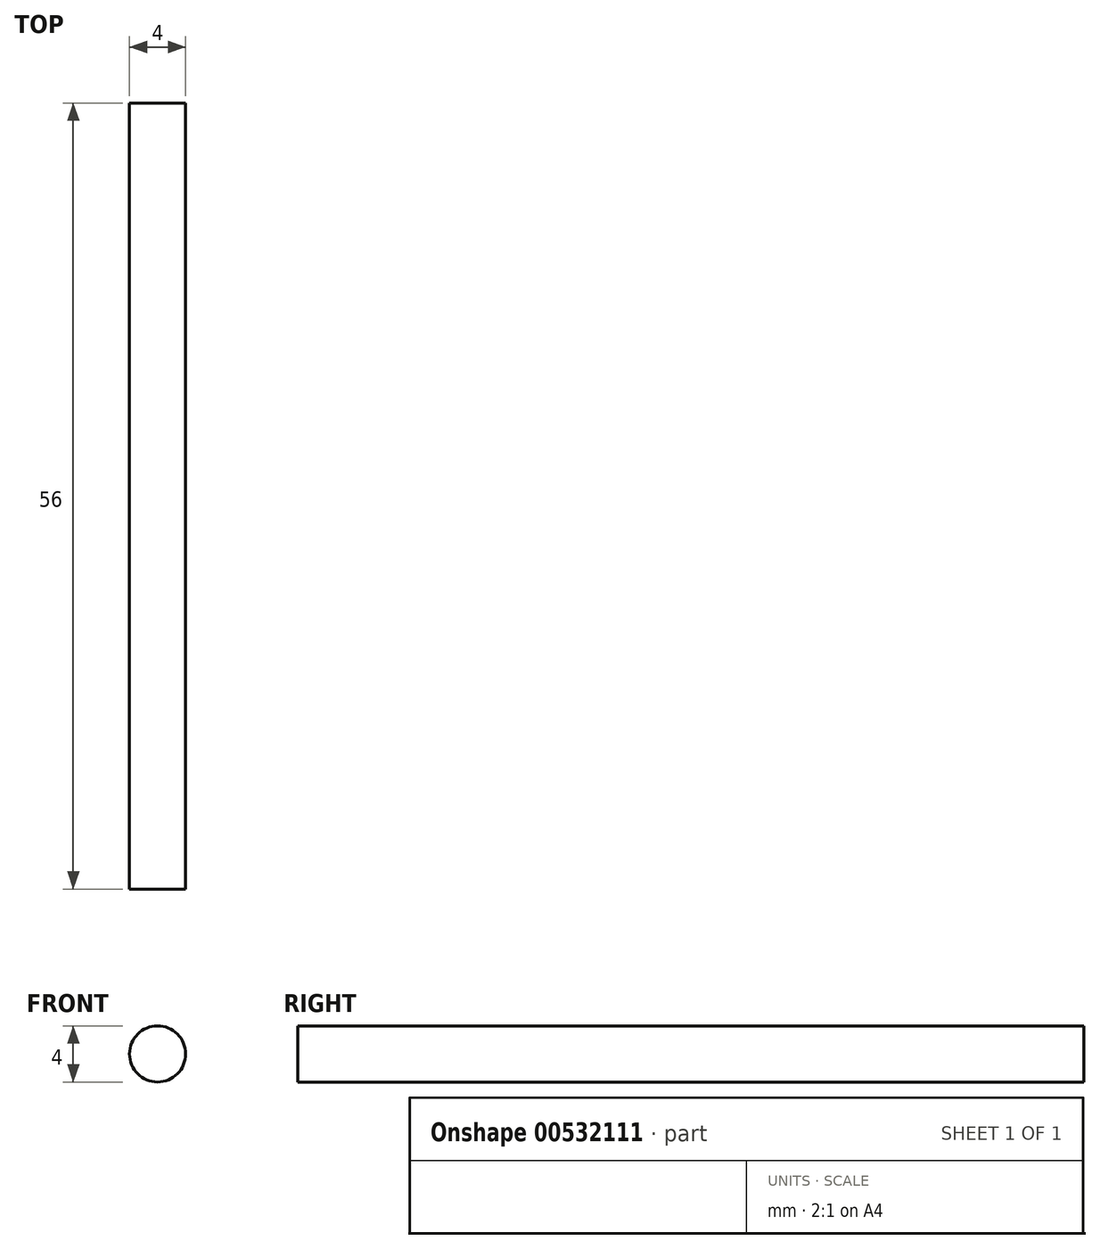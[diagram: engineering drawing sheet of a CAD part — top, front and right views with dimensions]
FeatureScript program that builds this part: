
annotation { "Feature Type Name" : "Feature", "Feature Type Description" : "" }
export const myFeature = defineFeature(function(context is Context, id is Id, definition is map)
    precondition{}
    {
        {
            var Q0;
            Q0=qCreatedBy(makeId("Front.planeOp"),FACE);
            var sketch = newSketch(context, id + "F0", { "sketchPlane" : qUnion([Q0])});
            skCircle(sketch, "E0", {"center": v(0, 0) * mm, "radius": 2 * mm});
            skSolve(sketch);
        }
        {
            var Q0;
            Q0 = qSketchRegion(id + "F0", true);
            extrude(context, id + "F1", {"entities" : qUnion([Q0]), "depth" : 56 * mm, "offsetDistance" : 25.4 * mm});
        }
    });
